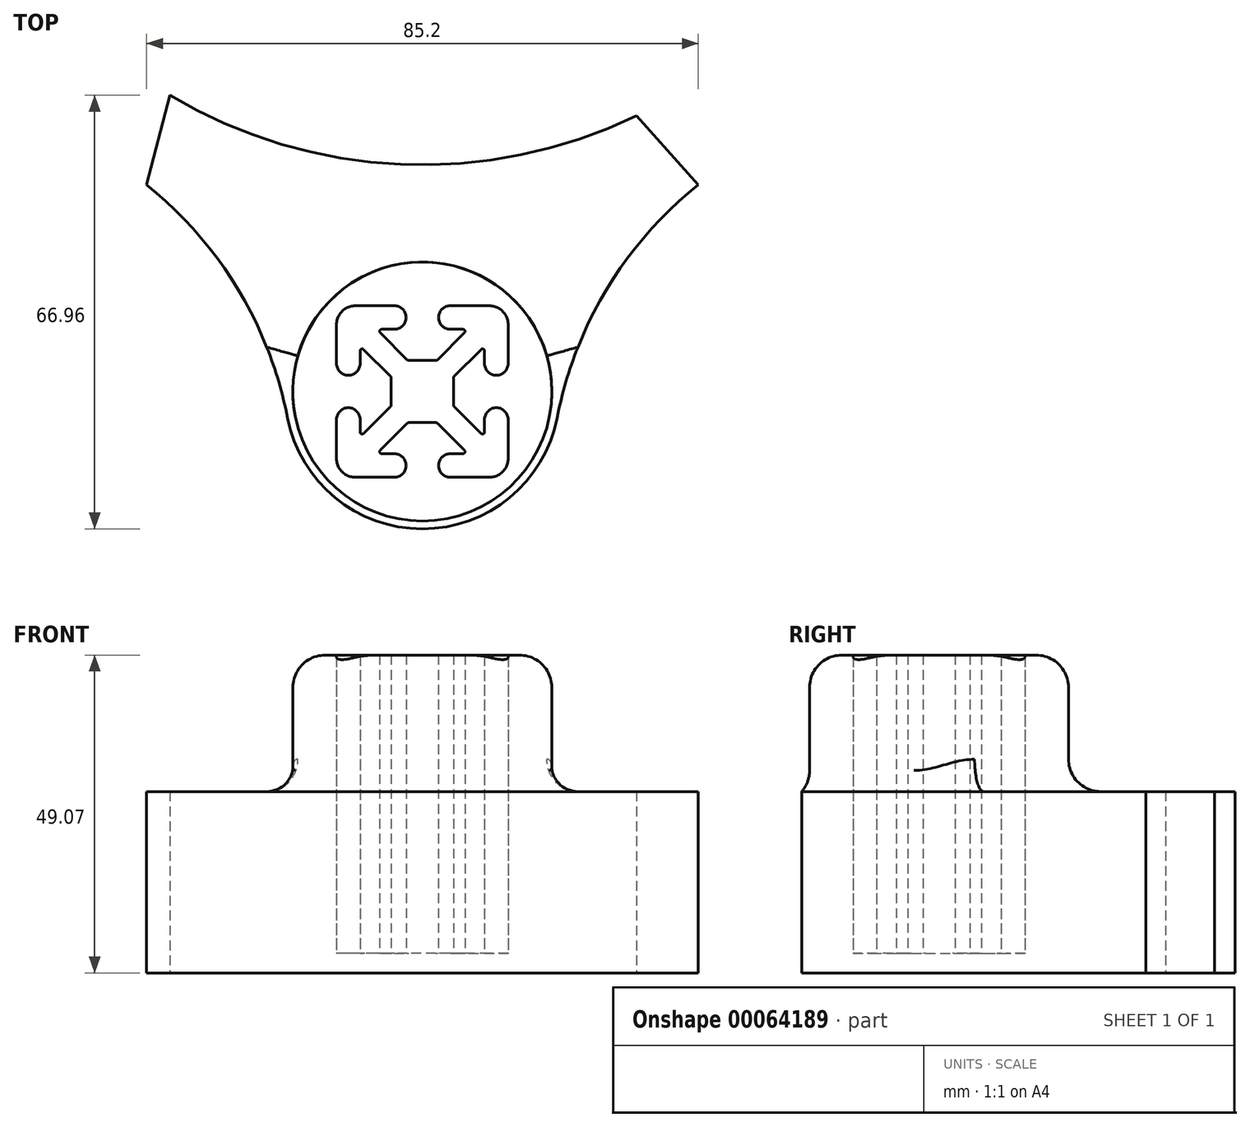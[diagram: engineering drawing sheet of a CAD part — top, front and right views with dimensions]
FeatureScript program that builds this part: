
annotation { "Feature Type Name" : "Feature", "Feature Type Description" : "" }
export const myFeature = defineFeature(function(context is Context, id is Id, definition is map)
    precondition{}
    {
        {
            var Q0;
            Q0=qCreatedBy(makeId("Top.planeOp"),FACE);
            var sketch = newSketch(context, id + "F0", { "sketchPlane" : qUnion([Q0])});
            skCircle(sketch, "E0", {"center": v(0, 0) * mm, "radius": 2.5 * mm});
            skLineSegment(sketch, "E1", {"start": v(0, 0) * mm, "end": v(0, 4.05) * mm, "construction": true});
            skLineSegment(sketch, "E2", {"start": v(0, 0) * mm, "end": v(-4.05, 0) * mm, "construction": true});
            skLineSegment(sketch, "E3", {"start": v(0, 0) * mm, "end": v(-12.5, 12.5) * mm, "construction": true});
            skLineSegment(sketch, "E4", {"start": v(-12.5, 10.36) * mm, "end": v(-12.5, 4.32) * mm});
            skLineSegment(sketch, "E5", {"start": v(-10.36, 12.5) * mm, "end": v(-4.32, 12.5) * mm});
            skLineSegment(sketch, "E6", {"start": v(-4.32, 10.36) * mm, "end": v(-6.26, 10.36) * mm});
            skLineSegment(sketch, "E7", {"start": v(-10.36, 6.26) * mm, "end": v(-10.36, 4.32) * mm});
            skArc(sketch, "E8", {"start": v(-4.32, 12.5) * mm, "mid": v(-3.25, 11.43) * mm, "end": v(-4.32, 10.36) * mm});
            skArc(sketch, "E9", {"start": v(-10.36, 4.32) * mm, "mid": v(-11.43, 3.25) * mm, "end": v(-12.5, 4.32) * mm});
            skLineSegment(sketch, "E10", {"start": v(0, 4.05) * mm, "end": v(-2.1, 4.05) * mm});
            skLineSegment(sketch, "E11", {"start": v(-4.05, 2.1) * mm, "end": v(-4.05, 0) * mm});
            skLineSegment(sketch, "E12", {"start": v(-8.53, 7.02) * mm, "end": v(-4.36, 2.85) * mm});
            skLineSegment(sketch, "E13", {"start": v(-7.02, 8.53) * mm, "end": v(-2.85, 4.36) * mm});
            skLineSegment(sketch, "E14.0.MirrorCS", {"start": v(10.36, 6.26) * mm, "end": v(10.36, 4.32) * mm});
            skLineSegment(sketch, "E14.1.MirrorCS", {"start": v(7.02, 8.53) * mm, "end": v(2.85, 4.36) * mm});
            skArc(sketch, "E14.2.MirrorCS", {"start": v(4.32, 12.5) * mm, "mid": v(3.25, 11.43) * mm, "end": v(4.32, 10.36) * mm});
            skArc(sketch, "E14.3.MirrorCS", {"start": v(10.36, 4.32) * mm, "mid": v(11.43, 3.25) * mm, "end": v(12.5, 4.32) * mm});
            skLineSegment(sketch, "E14.4.MirrorCS", {"start": v(10.36, 12.5) * mm, "end": v(4.32, 12.5) * mm});
            skLineSegment(sketch, "E14.5.MirrorCS", {"start": v(4.32, 10.36) * mm, "end": v(6.26, 10.36) * mm});
            skLineSegment(sketch, "E14.6.MirrorCS", {"start": v(12.5, 10.36) * mm, "end": v(12.5, 4.32) * mm});
            skLineSegment(sketch, "E14.7.MirrorCS", {"start": v(8.53, 7.02) * mm, "end": v(4.36, 2.85) * mm});
            skLineSegment(sketch, "E15.0.MirrorCS", {"start": v(0, 4.05) * mm, "end": v(2.1, 4.05) * mm});
            skLineSegment(sketch, "E16.0.MirrorCS", {"start": v(4.05, 2.1) * mm, "end": v(4.05, 0) * mm});
            skLineSegment(sketch, "E17.0.MirrorCS", {"start": v(10.36, -12.5) * mm, "end": v(4.32, -12.5) * mm});
            skLineSegment(sketch, "E17.1.MirrorCS", {"start": v(12.5, -10.36) * mm, "end": v(12.5, -4.32) * mm});
            skArc(sketch, "E17.2.MirrorCS", {"start": v(4.32, -12.5) * mm, "mid": v(3.25, -11.43) * mm, "end": v(4.32, -10.36) * mm});
            skLineSegment(sketch, "E17.3.MirrorCS", {"start": v(-7.02, -8.53) * mm, "end": v(-2.85, -4.36) * mm});
            skLineSegment(sketch, "E17.4.MirrorCS", {"start": v(7.02, -8.53) * mm, "end": v(2.85, -4.36) * mm});
            skLineSegment(sketch, "E17.5.MirrorCS", {"start": v(10.36, -6.26) * mm, "end": v(10.36, -4.32) * mm});
            skLineSegment(sketch, "E17.6.MirrorCS", {"start": v(8.53, -7.02) * mm, "end": v(4.36, -2.85) * mm});
            skLineSegment(sketch, "E17.7.MirrorCS", {"start": v(-10.36, -12.5) * mm, "end": v(-4.32, -12.5) * mm});
            skLineSegment(sketch, "E17.8.MirrorCS", {"start": v(-4.32, -10.36) * mm, "end": v(-6.26, -10.36) * mm});
            skLineSegment(sketch, "E17.9.MirrorCS", {"start": v(4.32, -10.36) * mm, "end": v(6.26, -10.36) * mm});
            skArc(sketch, "E17.10.MirrorCS", {"start": v(10.36, -4.32) * mm, "mid": v(11.43, -3.25) * mm, "end": v(12.5, -4.32) * mm});
            skLineSegment(sketch, "E17.11.MirrorCS", {"start": v(-12.5, -10.36) * mm, "end": v(-12.5, -4.32) * mm});
            skLineSegment(sketch, "E17.12.MirrorCS", {"start": v(0, -4.05) * mm, "end": v(2.1, -4.05) * mm});
            skArc(sketch, "E17.13.MirrorCS", {"start": v(-4.32, -12.5) * mm, "mid": v(-3.25, -11.43) * mm, "end": v(-4.32, -10.36) * mm});
            skLineSegment(sketch, "E17.14.MirrorCS", {"start": v(-8.53, -7.02) * mm, "end": v(-4.36, -2.85) * mm});
            skArc(sketch, "E17.15.MirrorCS", {"start": v(-10.36, -4.32) * mm, "mid": v(-11.43, -3.25) * mm, "end": v(-12.5, -4.32) * mm});
            skLineSegment(sketch, "E17.16.MirrorCS", {"start": v(-10.36, -6.26) * mm, "end": v(-10.36, -4.32) * mm});
            skLineSegment(sketch, "E17.17.MirrorCS", {"start": v(0, -4.05) * mm, "end": v(-2.1, -4.05) * mm});
            skLineSegment(sketch, "E18.0.MirrorCS", {"start": v(4.05, -2.1) * mm, "end": v(4.05, 0) * mm});
            skLineSegment(sketch, "E19.0.MirrorCS", {"start": v(-4.05, -2.1) * mm, "end": v(-4.05, 0) * mm});
            skPoint(sketch, "E20.visualSharp", {"position": v(-12.5, 12.5) * mm});
            skArc(sketch, "E20.filletArc", {"start": v(-10.36, 12.5) * mm, "mid": v(-11.87, 11.87) * mm, "end": v(-12.5, 10.36) * mm});
            skPoint(sketch, "E21.visualSharp", {"position": v(12.5, 12.5) * mm});
            skArc(sketch, "E21.filletArc", {"start": v(12.5, 10.36) * mm, "mid": v(11.87, 11.87) * mm, "end": v(10.36, 12.5) * mm});
            skPoint(sketch, "E22.visualSharp", {"position": v(12.5, -12.5) * mm});
            skArc(sketch, "E22.filletArc", {"start": v(10.36, -12.5) * mm, "mid": v(11.87, -11.87) * mm, "end": v(12.5, -10.36) * mm});
            skPoint(sketch, "E23.visualSharp", {"position": v(-12.5, -12.5) * mm});
            skArc(sketch, "E23.filletArc", {"start": v(-12.5, -10.36) * mm, "mid": v(-11.87, -11.87) * mm, "end": v(-10.36, -12.5) * mm});
            skPoint(sketch, "E24.visualSharp", {"position": v(4.05, 4.05) * mm});
            skPoint(sketch, "E25.visualSharp", {"position": v(-10.36, 8.85) * mm});
            skArc(sketch, "E25.filletArc", {"start": v(-8.53, 7.02) * mm, "mid": v(-9.7, 7.25) * mm, "end": v(-10.36, 6.26) * mm});
            skPoint(sketch, "E26.visualSharp", {"position": v(-8.85, 10.36) * mm});
            skArc(sketch, "E26.filletArc", {"start": v(-6.26, 10.36) * mm, "mid": v(-7.25, 9.7) * mm, "end": v(-7.02, 8.53) * mm});
            skPoint(sketch, "E27.visualSharp", {"position": v(8.85, 10.36) * mm});
            skArc(sketch, "E27.filletArc", {"start": v(7.02, 8.53) * mm, "mid": v(7.25, 9.7) * mm, "end": v(6.26, 10.36) * mm});
            skPoint(sketch, "E28.visualSharp", {"position": v(10.36, 8.85) * mm});
            skArc(sketch, "E28.filletArc", {"start": v(10.36, 6.26) * mm, "mid": v(9.7, 7.25) * mm, "end": v(8.53, 7.02) * mm});
            skPoint(sketch, "E29.visualSharp", {"position": v(10.36, -8.85) * mm});
            skArc(sketch, "E29.filletArc", {"start": v(8.53, -7.02) * mm, "mid": v(9.7, -7.25) * mm, "end": v(10.36, -6.26) * mm});
            skPoint(sketch, "E30.visualSharp", {"position": v(8.85, -10.36) * mm});
            skArc(sketch, "E30.filletArc", {"start": v(6.26, -10.36) * mm, "mid": v(7.25, -9.7) * mm, "end": v(7.02, -8.53) * mm});
            skPoint(sketch, "E31.visualSharp", {"position": v(-8.85, -10.36) * mm});
            skArc(sketch, "E31.filletArc", {"start": v(-7.02, -8.53) * mm, "mid": v(-7.25, -9.7) * mm, "end": v(-6.26, -10.36) * mm});
            skPoint(sketch, "E32.visualSharp", {"position": v(-10.36, -8.85) * mm});
            skArc(sketch, "E32.filletArc", {"start": v(-10.36, -6.26) * mm, "mid": v(-9.7, -7.25) * mm, "end": v(-8.53, -7.02) * mm});
            skPoint(sketch, "E33.orphan", {"position": v(-4.05, 4.05) * mm});
            skPoint(sketch, "E34.orphan", {"position": v(4.05, -4.05) * mm});
            skPoint(sketch, "E35.orphan", {"position": v(-4.05, -4.05) * mm});
            skPoint(sketch, "E36.visualSharp", {"position": v(-2.54, 4.05) * mm});
            skArc(sketch, "E36.filletArc", {"start": v(-2.85, 4.36) * mm, "mid": v(-2.5, 4.13) * mm, "end": v(-2.1, 4.05) * mm});
            skPoint(sketch, "E37.visualSharp", {"position": v(2.54, 4.05) * mm});
            skArc(sketch, "E37.filletArc", {"start": v(2.1, 4.05) * mm, "mid": v(2.5, 4.13) * mm, "end": v(2.85, 4.36) * mm});
            skPoint(sketch, "E38.visualSharp", {"position": v(-4.05, 2.54) * mm});
            skArc(sketch, "E38.filletArc", {"start": v(-4.05, 2.1) * mm, "mid": v(-4.13, 2.5) * mm, "end": v(-4.36, 2.85) * mm});
            skPoint(sketch, "E39.visualSharp", {"position": v(-4.05, -2.54) * mm});
            skArc(sketch, "E39.filletArc", {"start": v(-4.36, -2.85) * mm, "mid": v(-4.13, -2.5) * mm, "end": v(-4.05, -2.1) * mm});
            skPoint(sketch, "E40.visualSharp", {"position": v(-2.54, -4.05) * mm});
            skArc(sketch, "E40.filletArc", {"start": v(-2.1, -4.05) * mm, "mid": v(-2.5, -4.13) * mm, "end": v(-2.85, -4.36) * mm});
            skPoint(sketch, "E41.visualSharp", {"position": v(2.54, -4.05) * mm});
            skArc(sketch, "E41.filletArc", {"start": v(2.85, -4.36) * mm, "mid": v(2.5, -4.13) * mm, "end": v(2.1, -4.05) * mm});
            skPoint(sketch, "E42.visualSharp", {"position": v(4.05, -2.54) * mm});
            skArc(sketch, "E42.filletArc", {"start": v(4.05, -2.1) * mm, "mid": v(4.13, -2.5) * mm, "end": v(4.36, -2.85) * mm});
            skPoint(sketch, "E43.visualSharp", {"position": v(4.05, 2.54) * mm});
            skArc(sketch, "E43.filletArc", {"start": v(4.36, 2.85) * mm, "mid": v(4.13, 2.5) * mm, "end": v(4.05, 2.1) * mm});
            skSolve(sketch);
        }
        {
            var Q0;
            Q0=makeQuery(id+"F0.imprint","IMPRINT",FACE,{"disambiguationData":[TD([[makeQuery(id+"F0.imprint","IMPRINT",EDGE,{"derivedFrom":sQuery(id+"F0.wireOp",EDGE,"E0")}),-1.0]])]});
            var sketch = newSketch(context, id + "F1", { "sketchPlane" : qUnion([Q0])});
            skArc(sketch, "E44.0", {"start": v(-10.36, 13.25) * mm, "mid": v(-12.4, 12.4) * mm, "end": v(-13.25, 10.36) * mm});
            skLineSegment(sketch, "E44.1", {"start": v(-4.32, 13.25) * mm, "end": v(-10.36, 13.25) * mm});
            skArc(sketch, "E44.2", {"start": v(-4.32, 9.61) * mm, "mid": v(-2.5, 11.43) * mm, "end": v(-4.32, 13.25) * mm});
            skLineSegment(sketch, "E44.3", {"start": v(-6.26, 9.6) * mm, "end": v(-4.32, 9.61) * mm});
            skArc(sketch, "E44.4", {"start": v(-6.49, 9.06) * mm, "mid": v(-6.56, 9.41) * mm, "end": v(-6.26, 9.6) * mm});
            skLineSegment(sketch, "E44.5", {"start": v(-2.32, 4.9) * mm, "end": v(-6.49, 9.06) * mm});
            skArc(sketch, "E44.6", {"start": v(-2.1, 4.8) * mm, "mid": v(-2.22, 4.82) * mm, "end": v(-2.32, 4.9) * mm});
            skLineSegment(sketch, "E44.7", {"start": v(2.1, 4.8) * mm, "end": v(-2.1, 4.8) * mm});
            skArc(sketch, "E44.8", {"start": v(2.32, 4.9) * mm, "mid": v(2.22, 4.82) * mm, "end": v(2.1, 4.8) * mm});
            skLineSegment(sketch, "E44.9", {"start": v(6.49, 9.06) * mm, "end": v(2.32, 4.9) * mm});
            skArc(sketch, "E44.10", {"start": v(2.1, -4.8) * mm, "mid": v(2.22, -4.82) * mm, "end": v(2.32, -4.9) * mm});
            skLineSegment(sketch, "E44.11", {"start": v(-2.1, -4.8) * mm, "end": v(2.1, -4.8) * mm});
            skArc(sketch, "E44.12", {"start": v(-2.32, -4.9) * mm, "mid": v(-2.22, -4.82) * mm, "end": v(-2.1, -4.8) * mm});
            skLineSegment(sketch, "E44.13", {"start": v(-6.49, -9.06) * mm, "end": v(-2.32, -4.9) * mm});
            skArc(sketch, "E44.14", {"start": v(-6.26, -9.6) * mm, "mid": v(-6.56, -9.41) * mm, "end": v(-6.49, -9.06) * mm});
            skLineSegment(sketch, "E44.15", {"start": v(-4.32, -9.61) * mm, "end": v(-6.26, -9.61) * mm});
            skArc(sketch, "E44.16", {"start": v(-4.32, -13.25) * mm, "mid": v(-2.5, -11.43) * mm, "end": v(-4.32, -9.61) * mm});
            skLineSegment(sketch, "E44.17", {"start": v(-10.36, -13.25) * mm, "end": v(-4.32, -13.25) * mm});
            skArc(sketch, "E44.18", {"start": v(-13.25, -10.36) * mm, "mid": v(-12.4, -12.4) * mm, "end": v(-10.36, -13.25) * mm});
            skLineSegment(sketch, "E44.19", {"start": v(-13.25, -4.32) * mm, "end": v(-13.25, -10.36) * mm});
            skArc(sketch, "E44.20", {"start": v(-9.61, -4.32) * mm, "mid": v(-11.43, -2.5) * mm, "end": v(-13.25, -4.32) * mm});
            skLineSegment(sketch, "E44.21", {"start": v(-9.61, -6.26) * mm, "end": v(-9.61, -4.32) * mm});
            skArc(sketch, "E44.22", {"start": v(-9.61, 6.26) * mm, "mid": v(-9.41, 6.56) * mm, "end": v(-9.06, 6.49) * mm});
            skLineSegment(sketch, "E44.23", {"start": v(-9.61, 4.32) * mm, "end": v(-9.61, 6.26) * mm});
            skArc(sketch, "E44.24", {"start": v(-13.25, 4.32) * mm, "mid": v(-11.43, 2.5) * mm, "end": v(-9.61, 4.32) * mm});
            skLineSegment(sketch, "E44.25", {"start": v(-13.25, 10.36) * mm, "end": v(-13.25, 4.32) * mm});
            skLineSegment(sketch, "E44.26", {"start": v(-9.06, 6.49) * mm, "end": v(-4.9, 2.32) * mm});
            skArc(sketch, "E44.27", {"start": v(-4.9, 2.32) * mm, "mid": v(-4.82, 2.22) * mm, "end": v(-4.8, 2.1) * mm});
            skLineSegment(sketch, "E44.28", {"start": v(-4.8, 2.1) * mm, "end": v(-4.8, -2.1) * mm});
            skArc(sketch, "E44.29", {"start": v(-4.8, -2.1) * mm, "mid": v(-4.82, -2.22) * mm, "end": v(-4.9, -2.32) * mm});
            skLineSegment(sketch, "E44.30", {"start": v(-4.9, -2.32) * mm, "end": v(-9.06, -6.49) * mm});
            skArc(sketch, "E44.31", {"start": v(-9.06, -6.49) * mm, "mid": v(-9.41, -6.56) * mm, "end": v(-9.61, -6.26) * mm});
            skLineSegment(sketch, "E44.32", {"start": v(2.32, -4.9) * mm, "end": v(6.49, -9.06) * mm});
            skArc(sketch, "E44.33", {"start": v(6.49, -9.06) * mm, "mid": v(6.56, -9.41) * mm, "end": v(6.26, -9.61) * mm});
            skLineSegment(sketch, "E44.34", {"start": v(6.26, -9.61) * mm, "end": v(4.32, -9.61) * mm});
            skArc(sketch, "E44.35", {"start": v(4.32, -9.61) * mm, "mid": v(2.5, -11.43) * mm, "end": v(4.32, -13.25) * mm});
            skLineSegment(sketch, "E44.36", {"start": v(4.32, -13.25) * mm, "end": v(10.36, -13.25) * mm});
            skArc(sketch, "E44.37", {"start": v(10.36, -13.25) * mm, "mid": v(12.4, -12.4) * mm, "end": v(13.25, -10.36) * mm});
            skLineSegment(sketch, "E44.38", {"start": v(13.25, -10.36) * mm, "end": v(13.25, -4.32) * mm});
            skArc(sketch, "E44.39", {"start": v(13.25, -4.32) * mm, "mid": v(11.43, -2.5) * mm, "end": v(9.61, -4.32) * mm});
            skLineSegment(sketch, "E44.40", {"start": v(9.61, -4.32) * mm, "end": v(9.61, -6.26) * mm});
            skArc(sketch, "E44.41", {"start": v(9.61, -6.26) * mm, "mid": v(9.41, -6.56) * mm, "end": v(9.06, -6.49) * mm});
            skLineSegment(sketch, "E44.42", {"start": v(9.06, -6.49) * mm, "end": v(4.9, -2.32) * mm});
            skArc(sketch, "E44.43", {"start": v(4.9, -2.32) * mm, "mid": v(4.82, -2.22) * mm, "end": v(4.8, -2.1) * mm});
            skLineSegment(sketch, "E44.44", {"start": v(4.8, -2.1) * mm, "end": v(4.8, 2.1) * mm});
            skArc(sketch, "E44.45", {"start": v(4.8, 2.1) * mm, "mid": v(4.82, 2.22) * mm, "end": v(4.9, 2.32) * mm});
            skLineSegment(sketch, "E44.46", {"start": v(4.9, 2.32) * mm, "end": v(9.06, 6.49) * mm});
            skArc(sketch, "E44.47", {"start": v(9.06, 6.49) * mm, "mid": v(9.41, 6.56) * mm, "end": v(9.61, 6.26) * mm});
            skLineSegment(sketch, "E44.48", {"start": v(9.61, 6.26) * mm, "end": v(9.61, 4.32) * mm});
            skArc(sketch, "E44.49", {"start": v(9.61, 4.32) * mm, "mid": v(11.43, 2.5) * mm, "end": v(13.25, 4.32) * mm});
            skLineSegment(sketch, "E44.50", {"start": v(13.25, 4.32) * mm, "end": v(13.25, 10.36) * mm});
            skArc(sketch, "E44.51", {"start": v(13.25, 10.36) * mm, "mid": v(12.4, 12.4) * mm, "end": v(10.36, 13.25) * mm});
            skLineSegment(sketch, "E44.52", {"start": v(10.36, 13.25) * mm, "end": v(4.32, 13.25) * mm});
            skArc(sketch, "E44.53", {"start": v(4.32, 13.25) * mm, "mid": v(2.5, 11.43) * mm, "end": v(4.32, 9.61) * mm});
            skLineSegment(sketch, "E44.54", {"start": v(4.32, 9.61) * mm, "end": v(6.26, 9.61) * mm});
            skArc(sketch, "E44.55", {"start": v(6.26, 9.6) * mm, "mid": v(6.56, 9.41) * mm, "end": v(6.49, 9.06) * mm});
            skLineSegment(sketch, "E45.rect.bottom", {"start": v(15, -15) * mm, "end": v(-15, -15) * mm, "construction": true});
            skLineSegment(sketch, "E45.rect.top", {"start": v(15, 15) * mm, "end": v(-15, 15) * mm, "construction": true});
            skLineSegment(sketch, "E45.rect.left", {"start": v(15, -15) * mm, "end": v(15, 15) * mm, "construction": true});
            skLineSegment(sketch, "E45.rect.right", {"start": v(-15, -15) * mm, "end": v(-15, 15) * mm, "construction": true});
            skPoint(sketch, "E45.rect.middle", {"position": v(0, 0) * mm});
            skCircle(sketch, "E46", {"center": v(0, 0) * mm, "radius": 21.21 * mm});
            skCircle(sketch, "E47", {"center": v(0, 111.21) * mm, "radius": 90 * mm});
            skArc(sketch, "E48", {"start": v(42.6, 31.94) * mm, "mid": v(28.52, 15.87) * mm, "end": v(20.82, -4.06) * mm});
            skArc(sketch, "E49", {"start": v(-20.82, -4.06) * mm, "mid": v(-28.52, 15.87) * mm, "end": v(-42.6, 31.94) * mm});
            skCircle(sketch, "E50", {"center": v(0, 111.21) * mm, "radius": 76.2 * mm});
            skLineSegment(sketch, "E51", {"start": v(-42.6, 31.94) * mm, "end": v(-39, 45.75) * mm});
            skLineSegment(sketch, "E52", {"start": v(42.6, 31.94) * mm, "end": v(33.07, 42.56) * mm});
            skSolve(sketch);
        }
        {
            var Q0;
            Q0=makeQuery(id+"F1.imprint","IMPRINT",FACE,{"disambiguationData":[TD([[makeQuery(id+"F1.imprint","IMPRINT",EDGE,{"derivedFrom":makeQuery(id+"F0.imprint","IMPRINT",EDGE,{"derivedFrom":sQuery(id+"F0.wireOp",EDGE,"E0")})}),-1.0]])]});
            var Q1;
            Q1=makeQuery(id+"F1.imprint","IMPRINT",FACE,{"disambiguationData":[TD([[makeQuery(id+"F1.imprint","IMPRINT",EDGE,{"derivedFrom":sQuery(id+"F1.wireOp",EDGE,"E44.0")}),-1.0]])]});
            var Q2;
            Q2=makeQuery(id+"F1.imprint","IMPRINT",FACE,{"disambiguationData":[TD([[makeQuery(id+"F1.imprint","IMPRINT",EDGE,{"derivedFrom":makeQuery(id+"F0.imprint","IMPRINT",EDGE,{"derivedFrom":sQuery(id+"F0.wireOp",EDGE,"E0")})}),1.0]])]});
            var Q3;
            Q3=makeQuery(id+"F1.imprint","IMPRINT",FACE,{"disambiguationData":[TD([[makeQuery(id+"F1.imprint","IMPRINT",EDGE,{"derivedFrom":sQuery(id+"F1.wireOp",EDGE,"E44.0")}),1.0]])]});
            var Q4;
            {var subQ0=sQuery(id+"F1.wireOp",EDGE,"E48");Q4=makeQuery(id+"F1.imprint","IMPRINT",FACE,{"disambiguationData":[TD([[makeQuery(id+"F1.imprint","IMPRINT",EDGE,{"derivedFrom":subQ0}),-1.0]])]});}
            var Q5;
            {var subQ0=sQuery(id+"F1.wireOp",EDGE,"2fe30f52-9815-44ae-bf93-b81bc341cbbc");Q5=makeQuery(id+"F1.imprint","IMPRINT",FACE,{"disambiguationData":[TD([[makeQuery(id+"F1.imprint","IMPRINT",EDGE,{"derivedFrom":subQ0}),-1.0]])]});}
            var Q6;
            {var subQ0=sQuery(id+"F1.wireOp",EDGE,"E49");Q6=makeQuery(id+"F1.imprint","IMPRINT",FACE,{"disambiguationData":[TD([[makeQuery(id+"F1.imprint","IMPRINT",EDGE,{"derivedFrom":subQ0}),-1.0]])]});}
            var Q7;
            {var subQ0=sQuery(id+"F1.wireOp",EDGE,"E51");Q7=makeQuery(id+"F1.imprint","IMPRINT",FACE,{"disambiguationData":[TD([[makeQuery(id+"F1.imprint","IMPRINT",EDGE,{"derivedFrom":subQ0}),-1.0]])]});}
            extrude(context, id + "F2", {"entities" : qUnion([Q0, Q1, Q2, Q3, Q4, Q5, Q6, Q7]), "depth" : 3 * mm});
        }
        {
            var Q0;
            Q0=makeQuery(id+"F2.opExtrude","CAP_FACE",FACE,{"disambiguationData":[OSD([sQuery(id+"F1.wireOp",EDGE,"E46"),sQuery(id+"F1.wireOp",EDGE,"E47"),sQuery(id+"F1.wireOp",EDGE,"E48"),sQuery(id+"F1.wireOp",EDGE,"2fe30f52-9815-44ae-bf93-b81bc341cbbc")])],"isStart":false});
            var sketch = newSketch(context, id + "F3", { "sketchPlane" : qUnion([Q0])});
            skLineSegment(sketch, "E53.0", {"start": v(-13.25, 10.36) * mm, "end": v(-13.25, 4.32) * mm});
            skArc(sketch, "E53.1", {"start": v(-10.36, 13.25) * mm, "mid": v(-12.4, 12.4) * mm, "end": v(-13.25, 10.36) * mm});
            skArc(sketch, "E53.2", {"start": v(-4.32, -13.25) * mm, "mid": v(-2.5, -11.43) * mm, "end": v(-4.32, -9.61) * mm});
            skLineSegment(sketch, "E53.3", {"start": v(-10.36, -13.25) * mm, "end": v(-4.32, -13.25) * mm});
            skArc(sketch, "E53.4", {"start": v(-13.25, -10.36) * mm, "mid": v(-12.4, -12.4) * mm, "end": v(-10.36, -13.25) * mm});
            skLineSegment(sketch, "E53.5", {"start": v(-13.25, -4.32) * mm, "end": v(-13.25, -10.36) * mm});
            skArc(sketch, "E53.6", {"start": v(-9.61, -4.32) * mm, "mid": v(-11.43, -2.5) * mm, "end": v(-13.25, -4.32) * mm});
            skLineSegment(sketch, "E53.7", {"start": v(-4.9, -2.32) * mm, "end": v(-9.06, -6.49) * mm});
            skLineSegment(sketch, "E53.8", {"start": v(-9.61, -6.26) * mm, "end": v(-9.61, -4.32) * mm});
            skArc(sketch, "E53.9", {"start": v(-9.06, -6.49) * mm, "mid": v(-9.41, -6.56) * mm, "end": v(-9.61, -6.26) * mm});
            skLineSegment(sketch, "E53.10", {"start": v(-4.32, -9.61) * mm, "end": v(-6.26, -9.61) * mm});
            skArc(sketch, "E53.11", {"start": v(-6.26, -9.6) * mm, "mid": v(-6.56, -9.41) * mm, "end": v(-6.49, -9.06) * mm});
            skLineSegment(sketch, "E53.12", {"start": v(-6.49, -9.06) * mm, "end": v(-2.32, -4.9) * mm});
            skLineSegment(sketch, "E53.13", {"start": v(-2.1, -4.8) * mm, "end": v(2.1, -4.8) * mm});
            skArc(sketch, "E53.14", {"start": v(-2.32, -4.9) * mm, "mid": v(-2.22, -4.82) * mm, "end": v(-2.1, -4.8) * mm});
            skArc(sketch, "E53.15", {"start": v(-4.8, -2.1) * mm, "mid": v(-4.82, -2.22) * mm, "end": v(-4.9, -2.32) * mm});
            skLineSegment(sketch, "E53.16", {"start": v(-4.8, 2.1) * mm, "end": v(-4.8, -2.1) * mm});
            skArc(sketch, "E53.17", {"start": v(-13.25, 4.32) * mm, "mid": v(-11.43, 2.5) * mm, "end": v(-9.61, 4.32) * mm});
            skLineSegment(sketch, "E53.18", {"start": v(-9.61, 4.32) * mm, "end": v(-9.61, 6.26) * mm});
            skArc(sketch, "E53.19", {"start": v(-9.61, 6.26) * mm, "mid": v(-9.41, 6.56) * mm, "end": v(-9.06, 6.49) * mm});
            skLineSegment(sketch, "E53.20", {"start": v(-9.06, 6.49) * mm, "end": v(-4.9, 2.32) * mm});
            skArc(sketch, "E53.21", {"start": v(-4.9, 2.32) * mm, "mid": v(-4.82, 2.22) * mm, "end": v(-4.8, 2.1) * mm});
            skLineSegment(sketch, "E53.22", {"start": v(-4.32, 13.25) * mm, "end": v(-10.36, 13.25) * mm});
            skArc(sketch, "E53.23", {"start": v(-4.32, 9.61) * mm, "mid": v(-2.5, 11.43) * mm, "end": v(-4.32, 13.25) * mm});
            skLineSegment(sketch, "E53.24", {"start": v(-6.26, 9.6) * mm, "end": v(-4.32, 9.61) * mm});
            skArc(sketch, "E53.25", {"start": v(-6.49, 9.06) * mm, "mid": v(-6.56, 9.41) * mm, "end": v(-6.26, 9.6) * mm});
            skLineSegment(sketch, "E53.26", {"start": v(-2.32, 4.9) * mm, "end": v(-6.49, 9.06) * mm});
            skLineSegment(sketch, "E53.27", {"start": v(2.1, 4.8) * mm, "end": v(-2.1, 4.8) * mm});
            skArc(sketch, "E53.28", {"start": v(-2.1, 4.8) * mm, "mid": v(-2.22, 4.82) * mm, "end": v(-2.32, 4.9) * mm});
            skArc(sketch, "E53.29", {"start": v(2.32, 4.9) * mm, "mid": v(2.22, 4.82) * mm, "end": v(2.1, 4.8) * mm});
            skLineSegment(sketch, "E53.30", {"start": v(6.49, 9.06) * mm, "end": v(2.32, 4.9) * mm});
            skArc(sketch, "E53.31", {"start": v(6.26, 9.6) * mm, "mid": v(6.56, 9.41) * mm, "end": v(6.49, 9.06) * mm});
            skLineSegment(sketch, "E53.32", {"start": v(4.32, 9.61) * mm, "end": v(6.26, 9.61) * mm});
            skArc(sketch, "E53.33", {"start": v(4.32, 13.25) * mm, "mid": v(2.5, 11.43) * mm, "end": v(4.32, 9.61) * mm});
            skLineSegment(sketch, "E53.34", {"start": v(10.36, 13.25) * mm, "end": v(4.32, 13.25) * mm});
            skArc(sketch, "E53.35", {"start": v(13.25, 10.36) * mm, "mid": v(12.4, 12.4) * mm, "end": v(10.36, 13.25) * mm});
            skLineSegment(sketch, "E53.36", {"start": v(13.25, 4.32) * mm, "end": v(13.25, 10.36) * mm});
            skArc(sketch, "E53.37", {"start": v(9.61, 4.32) * mm, "mid": v(11.43, 2.5) * mm, "end": v(13.25, 4.32) * mm});
            skLineSegment(sketch, "E53.38", {"start": v(9.61, 6.26) * mm, "end": v(9.61, 4.32) * mm});
            skLineSegment(sketch, "E53.39", {"start": v(4.9, 2.32) * mm, "end": v(9.06, 6.49) * mm});
            skArc(sketch, "E53.40", {"start": v(9.06, 6.49) * mm, "mid": v(9.41, 6.56) * mm, "end": v(9.61, 6.26) * mm});
            skLineSegment(sketch, "E53.41", {"start": v(4.8, -2.1) * mm, "end": v(4.8, 2.1) * mm});
            skArc(sketch, "E53.42", {"start": v(4.8, 2.1) * mm, "mid": v(4.82, 2.22) * mm, "end": v(4.9, 2.32) * mm});
            skArc(sketch, "E53.44", {"start": v(4.9, -2.32) * mm, "mid": v(4.82, -2.22) * mm, "end": v(4.8, -2.1) * mm});
            skLineSegment(sketch, "E53.45", {"start": v(9.06, -6.49) * mm, "end": v(4.9, -2.32) * mm});
            skLineSegment(sketch, "E53.46", {"start": v(2.32, -4.9) * mm, "end": v(6.49, -9.06) * mm});
            skArc(sketch, "E53.47", {"start": v(4.32, -9.61) * mm, "mid": v(2.5, -11.43) * mm, "end": v(4.32, -13.25) * mm});
            skLineSegment(sketch, "E53.48", {"start": v(4.32, -13.25) * mm, "end": v(10.36, -13.25) * mm});
            skArc(sketch, "E53.49", {"start": v(10.36, -13.25) * mm, "mid": v(12.4, -12.4) * mm, "end": v(13.25, -10.36) * mm});
            skLineSegment(sketch, "E53.50", {"start": v(13.25, -10.36) * mm, "end": v(13.25, -4.32) * mm});
            skArc(sketch, "E53.51", {"start": v(13.25, -4.32) * mm, "mid": v(11.43, -2.5) * mm, "end": v(9.61, -4.32) * mm});
            skLineSegment(sketch, "E53.52", {"start": v(9.61, -4.32) * mm, "end": v(9.61, -6.26) * mm});
            skArc(sketch, "E53.53", {"start": v(9.61, -6.26) * mm, "mid": v(9.41, -6.56) * mm, "end": v(9.06, -6.49) * mm});
            skArc(sketch, "E53.54", {"start": v(6.49, -9.06) * mm, "mid": v(6.56, -9.41) * mm, "end": v(6.26, -9.61) * mm});
            skLineSegment(sketch, "E53.55", {"start": v(6.26, -9.61) * mm, "end": v(4.32, -9.61) * mm});
            skArc(sketch, "E53.56", {"start": v(2.1, -4.8) * mm, "mid": v(2.22, -4.82) * mm, "end": v(2.32, -4.9) * mm});
            skSolve(sketch);
        }
        {
            var Q0;
            Q0=makeQuery(id+"F3.imprint","IMPRINT",FACE,{"disambiguationData":[TD([[makeQuery(id+"F3.imprint","IMPRINT",EDGE,{"derivedFrom":sQuery(id+"F3.wireOp",EDGE,"E53.0")}),-1.0]])]});
            extrude(context, id + "F4", {"entities" : qUnion([Q0]), "operationType" : NewBodyOperationType.ADD, "depth" : 25 * mm});
        }
        {
            var Q0;
            Q0=makeQuery(id+"F4.opExtrude","CAP_FACE",FACE,{"disambiguationData":[OSD([sQuery(id+"F1.wireOp",EDGE,"E46"),sQuery(id+"F1.wireOp",EDGE,"E47"),sQuery(id+"F1.wireOp",EDGE,"E48"),sQuery(id+"F1.wireOp",EDGE,"2fe30f52-9815-44ae-bf93-b81bc341cbbc"),sQuery(id+"F3.wireOp",EDGE,"E53.0"),sQuery(id+"F3.wireOp",EDGE,"E53.1"),sQuery(id+"F3.wireOp",EDGE,"E53.2"),sQuery(id+"F3.wireOp",EDGE,"E53.3"),sQuery(id+"F3.wireOp",EDGE,"E53.4"),sQuery(id+"F3.wireOp",EDGE,"E53.5"),sQuery(id+"F3.wireOp",EDGE,"E53.6"),sQuery(id+"F3.wireOp",EDGE,"E53.7"),sQuery(id+"F3.wireOp",EDGE,"E53.8"),sQuery(id+"F3.wireOp",EDGE,"E53.9"),sQuery(id+"F3.wireOp",EDGE,"E53.10"),sQuery(id+"F3.wireOp",EDGE,"E53.11"),sQuery(id+"F3.wireOp",EDGE,"E53.12"),sQuery(id+"F3.wireOp",EDGE,"E53.13"),sQuery(id+"F3.wireOp",EDGE,"E53.14"),sQuery(id+"F3.wireOp",EDGE,"E53.15"),sQuery(id+"F3.wireOp",EDGE,"E53.16"),sQuery(id+"F3.wireOp",EDGE,"E53.17"),sQuery(id+"F3.wireOp",EDGE,"E53.18"),sQuery(id+"F3.wireOp",EDGE,"E53.19"),sQuery(id+"F3.wireOp",EDGE,"E53.20"),sQuery(id+"F3.wireOp",EDGE,"E53.21"),sQuery(id+"F3.wireOp",EDGE,"E53.22"),sQuery(id+"F3.wireOp",EDGE,"E53.23"),sQuery(id+"F3.wireOp",EDGE,"E53.24"),sQuery(id+"F3.wireOp",EDGE,"E53.25"),sQuery(id+"F3.wireOp",EDGE,"E53.26"),sQuery(id+"F3.wireOp",EDGE,"E53.27"),sQuery(id+"F3.wireOp",EDGE,"E53.28"),sQuery(id+"F3.wireOp",EDGE,"E53.29"),sQuery(id+"F3.wireOp",EDGE,"E53.30"),sQuery(id+"F3.wireOp",EDGE,"E53.31"),sQuery(id+"F3.wireOp",EDGE,"E53.32"),sQuery(id+"F3.wireOp",EDGE,"E53.33"),sQuery(id+"F3.wireOp",EDGE,"E53.34"),sQuery(id+"F3.wireOp",EDGE,"E53.35"),sQuery(id+"F3.wireOp",EDGE,"E53.36"),sQuery(id+"F3.wireOp",EDGE,"E53.37"),sQuery(id+"F3.wireOp",EDGE,"E53.38"),sQuery(id+"F3.wireOp",EDGE,"E53.39"),sQuery(id+"F3.wireOp",EDGE,"E53.40"),sQuery(id+"F3.wireOp",EDGE,"E53.41"),sQuery(id+"F3.wireOp",EDGE,"E53.42"),sQuery(id+"F3.wireOp",EDGE,"E53.44"),sQuery(id+"F3.wireOp",EDGE,"E53.45"),sQuery(id+"F3.wireOp",EDGE,"E53.46"),sQuery(id+"F3.wireOp",EDGE,"E53.47"),sQuery(id+"F3.wireOp",EDGE,"E53.48"),sQuery(id+"F3.wireOp",EDGE,"E53.49"),sQuery(id+"F3.wireOp",EDGE,"E53.50"),sQuery(id+"F3.wireOp",EDGE,"E53.51"),sQuery(id+"F3.wireOp",EDGE,"E53.52"),sQuery(id+"F3.wireOp",EDGE,"E53.53"),sQuery(id+"F3.wireOp",EDGE,"E53.54"),sQuery(id+"F3.wireOp",EDGE,"E53.55"),sQuery(id+"F3.wireOp",EDGE,"E53.56")])],"isStart":false});
            var sketch = newSketch(context, id + "F5", { "sketchPlane" : qUnion([Q0])});
            skCircle(sketch, "E54", {"center": v(0, 0) * mm, "radius": 20 * mm});
            skSolve(sketch);
        }
        {
            var Q0;
            {var subQ5=makeQuery(id+"F4.opExtrude","CAP_EDGE",EDGE,{"disambiguationData":[OSD([sQuery(id+"F3.wireOp",EDGE,"E53.36")])],"isStart":false});Q0=makeQuery(id+"F5.imprint","IMPRINT",FACE,{"disambiguationData":[TD([[makeQuery(id+"F5.imprint","IMPRINT",EDGE,{"derivedFrom":subQ5}),-1.0]])]});}
            var Q1;
            {var subQ0=makeQuery(id+"F4.opExtrude","CAP_EDGE",EDGE,{"disambiguationData":[OSD([sQuery(id+"F3.wireOp",EDGE,"E53.22")])],"isStart":false});Q1=makeQuery(id+"F5.imprint","IMPRINT",FACE,{"disambiguationData":[TD([[makeQuery(id+"F5.imprint","IMPRINT",EDGE,{"derivedFrom":subQ0}),-1.0]])]});}
            var Q2;
            {var subQ1=makeQuery(id+"F4.opExtrude","CAP_EDGE",EDGE,{"disambiguationData":[OSD([sQuery(id+"F3.wireOp",EDGE,"E53.0")])],"isStart":false});Q2=makeQuery(id+"F5.imprint","IMPRINT",FACE,{"disambiguationData":[TD([[makeQuery(id+"F5.imprint","IMPRINT",EDGE,{"derivedFrom":subQ1}),-1.0]])]});}
            var Q3;
            Q3=makeQuery(id+"F5.imprint","IMPRINT",FACE,{"disambiguationData":[TD([[makeQuery(id+"F5.imprint","IMPRINT",EDGE,{"derivedFrom":makeQuery(id+"F4.opExtrude","CAP_EDGE",EDGE,{"disambiguationData":[OSD([sQuery(id+"F3.wireOp",EDGE,"E53.2")])],"isStart":false})}),-1.0]])]});
            extrude(context, id + "F6", {"entities" : qUnion([Q0, Q1, Q2, Q3]), "operationType" : NewBodyOperationType.ADD, "endBound" : BoundingType.SYMMETRIC, "depth" : 42.15 * mm});
        }
        {
            var Q0;
            Q0=makeQuery(id+"F6.opExtrude","CAP_EDGE",EDGE,{"disambiguationData":[OSD([sQuery(id+"F5.wireOp",EDGE,"E54")])],"isStart":false});
            fillet(context, id + "F7", {"entities" : qUnion([Q0]), "radius" : 5 * mm, "tangentPropagation" : true, "allowEdgeOverflow" : false});
        }
        {
            var Q0;
            Q0=makeQuery(id+"F6.boolean.opBoolean","INTERSECT",EDGE,{"derivedFrom":[makeQuery(id+"F4.opExtrude","CAP_FACE",FACE,{"disambiguationData":[OSD([sQuery(id+"F1.wireOp",EDGE,"E46"),sQuery(id+"F1.wireOp",EDGE,"E47"),sQuery(id+"F1.wireOp",EDGE,"E48"),sQuery(id+"F3.wireOp",EDGE,"E53.0"),sQuery(id+"F3.wireOp",EDGE,"E53.1"),sQuery(id+"F3.wireOp",EDGE,"E53.2"),sQuery(id+"F3.wireOp",EDGE,"E53.3"),sQuery(id+"F3.wireOp",EDGE,"E53.4"),sQuery(id+"F3.wireOp",EDGE,"E53.5"),sQuery(id+"F3.wireOp",EDGE,"E53.6"),sQuery(id+"F3.wireOp",EDGE,"E53.7"),sQuery(id+"F3.wireOp",EDGE,"E53.8"),sQuery(id+"F3.wireOp",EDGE,"E53.9"),sQuery(id+"F3.wireOp",EDGE,"E53.10"),sQuery(id+"F3.wireOp",EDGE,"E53.11"),sQuery(id+"F3.wireOp",EDGE,"E53.12"),sQuery(id+"F3.wireOp",EDGE,"E53.13"),sQuery(id+"F3.wireOp",EDGE,"E53.14"),sQuery(id+"F3.wireOp",EDGE,"E53.15"),sQuery(id+"F3.wireOp",EDGE,"E53.16"),sQuery(id+"F3.wireOp",EDGE,"E53.17"),sQuery(id+"F3.wireOp",EDGE,"E53.18"),sQuery(id+"F3.wireOp",EDGE,"E53.19"),sQuery(id+"F3.wireOp",EDGE,"E53.20"),sQuery(id+"F3.wireOp",EDGE,"E53.21"),sQuery(id+"F3.wireOp",EDGE,"E53.22"),sQuery(id+"F3.wireOp",EDGE,"E53.23"),sQuery(id+"F3.wireOp",EDGE,"E53.24"),sQuery(id+"F3.wireOp",EDGE,"E53.25"),sQuery(id+"F3.wireOp",EDGE,"E53.26"),sQuery(id+"F3.wireOp",EDGE,"E53.27"),sQuery(id+"F3.wireOp",EDGE,"E53.28"),sQuery(id+"F3.wireOp",EDGE,"E53.29"),sQuery(id+"F3.wireOp",EDGE,"E53.30"),sQuery(id+"F3.wireOp",EDGE,"E53.31"),sQuery(id+"F3.wireOp",EDGE,"E53.32"),sQuery(id+"F3.wireOp",EDGE,"E53.33"),sQuery(id+"F3.wireOp",EDGE,"E53.34"),sQuery(id+"F3.wireOp",EDGE,"E53.35"),sQuery(id+"F3.wireOp",EDGE,"E53.36"),sQuery(id+"F3.wireOp",EDGE,"E53.37"),sQuery(id+"F3.wireOp",EDGE,"E53.38"),sQuery(id+"F3.wireOp",EDGE,"E53.39"),sQuery(id+"F3.wireOp",EDGE,"E53.40"),sQuery(id+"F3.wireOp",EDGE,"E53.41"),sQuery(id+"F3.wireOp",EDGE,"E53.42"),sQuery(id+"F3.wireOp",EDGE,"E53.44"),sQuery(id+"F3.wireOp",EDGE,"E53.45"),sQuery(id+"F3.wireOp",EDGE,"E53.46"),sQuery(id+"F3.wireOp",EDGE,"E53.47"),sQuery(id+"F3.wireOp",EDGE,"E53.48"),sQuery(id+"F3.wireOp",EDGE,"E53.49"),sQuery(id+"F3.wireOp",EDGE,"E53.50"),sQuery(id+"F3.wireOp",EDGE,"E53.51"),sQuery(id+"F3.wireOp",EDGE,"E53.52"),sQuery(id+"F3.wireOp",EDGE,"E53.53"),sQuery(id+"F3.wireOp",EDGE,"E53.54"),sQuery(id+"F3.wireOp",EDGE,"E53.55"),sQuery(id+"F3.wireOp",EDGE,"E53.56")])],"isStart":false}),makeQuery(id+"F6.opExtrude","SWEPT_FACE",FACE,{"disambiguationData":[OSD([sQuery(id+"F5.wireOp",EDGE,"E54")])]})]});
            fillet(context, id + "F8", {"entities" : qUnion([Q0]), "radius" : 5 * mm, "tangentPropagation" : true, "allowEdgeOverflow" : false});
        }
    });
